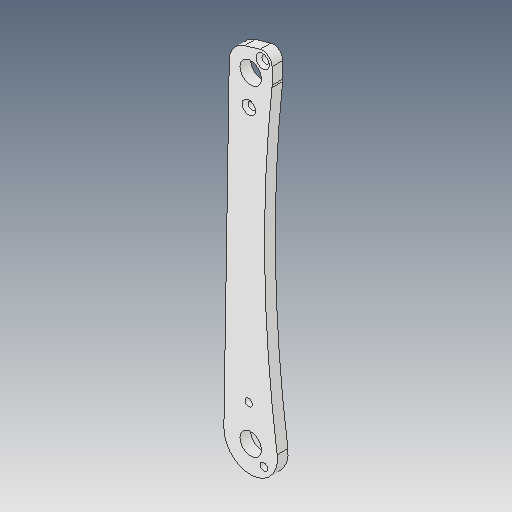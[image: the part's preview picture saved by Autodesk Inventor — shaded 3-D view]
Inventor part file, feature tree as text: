
AUTODESK INVENTOR PART (.ipt)
format: ipt  version: 2019.4 (Build 234330000, 330)  size: 137,728 bytes
history: native  units: mm
features: hole x3, sketch x2, other x1, extrude x1
ambient origin geometry x8: Origin, YZ Plane, XZ Plane, XY Plane, X Axis, Y Axis, Z Axis, Center Point
bodies: Body1 (feature_tree)
feature tree (7):
  other  "ソリッド1"
  sketch  "スケッチ1"
  extrude  "押し出し1"  Depth=60.0mm
  hole  "穴1"  [1 undecoded]
  hole  "穴2"  [1 undecoded]
  hole  "穴4"  [1 undecoded]
  sketch  "スケッチ2"
note: 3 required parameter values undecoded (feature->parameter linkage not recoverable at this tier; creation-order binding heuristic only, values carry confidence <= 0.55)
